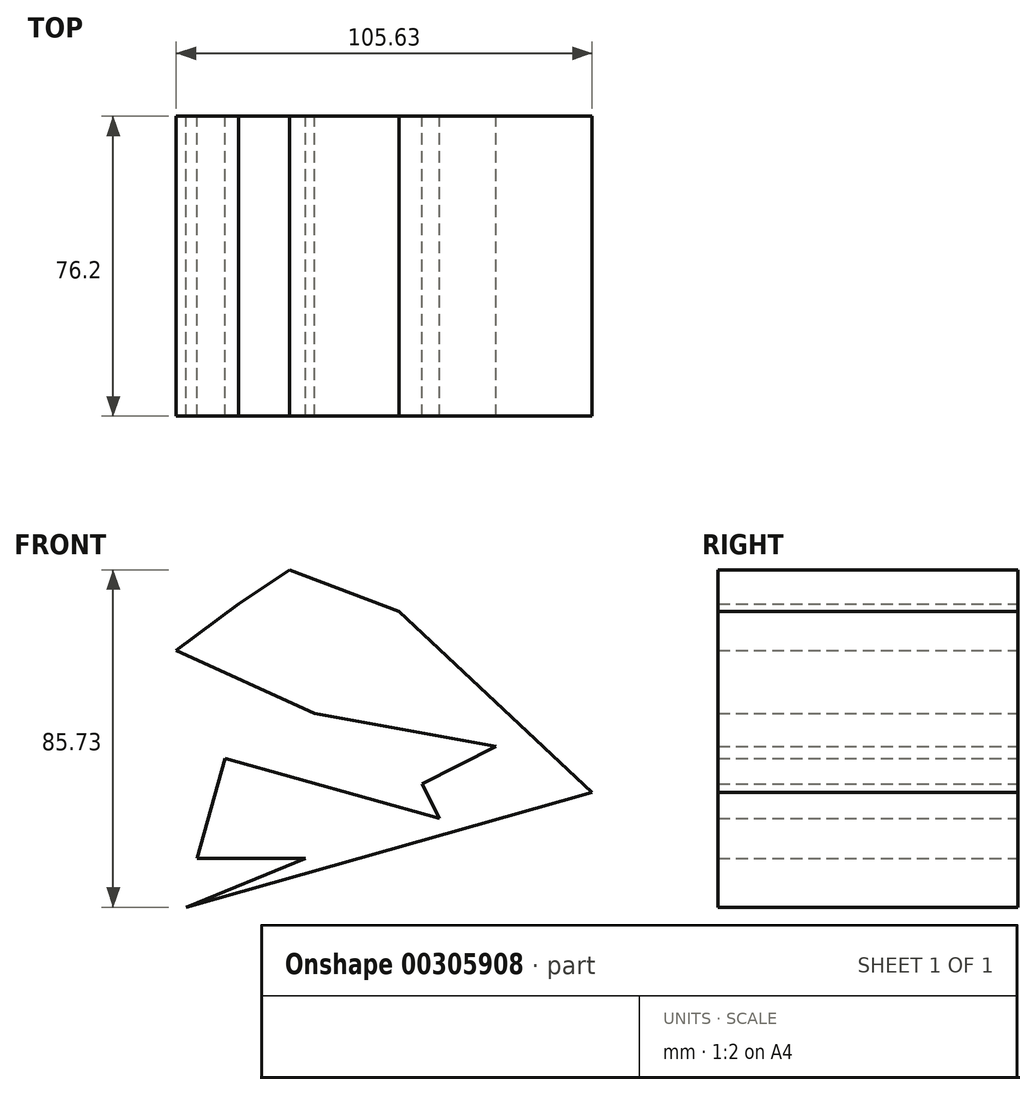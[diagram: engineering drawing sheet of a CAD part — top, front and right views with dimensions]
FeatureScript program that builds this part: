
annotation { "Feature Type Name" : "Feature", "Feature Type Description" : "" }
export const myFeature = defineFeature(function(context is Context, id is Id, definition is map)
    precondition{}
    {
        {
            var Q0;
            Q0=qCreatedBy(makeId("Front.planeOp"),FACE);
            var sketch = newSketch(context, id + "F0", { "sketchPlane" : qUnion([Q0])});
            skLineSegment(sketch, "E0", {"start": v(-44.24, -35.77) * mm, "end": v(58.83, -6.6) * mm});
            skLineSegment(sketch, "E1", {"start": v(58.83, -6.6) * mm, "end": v(9.75, 39.32) * mm});
            skLineSegment(sketch, "E2", {"start": v(9.75, 39.32) * mm, "end": v(-18.03, 49.96) * mm});
            skLineSegment(sketch, "E3", {"start": v(-18.03, 49.96) * mm, "end": v(-31.04, 41.29) * mm});
            skLineSegment(sketch, "E4", {"start": v(-31.04, 41.29) * mm, "end": v(-46.8, 29.46) * mm});
            skLineSegment(sketch, "E5", {"start": v(-46.8, 29.46) * mm, "end": v(-11.73, 13.5) * mm});
            skLineSegment(sketch, "E6", {"start": v(-11.73, 13.5) * mm, "end": v(34.4, 5.03) * mm});
            skLineSegment(sketch, "E7", {"start": v(34.4, 5.03) * mm, "end": v(15.67, -4.43) * mm});
            skLineSegment(sketch, "E8", {"start": v(15.67, -4.43) * mm, "end": v(20.12, -13.25) * mm});
            skLineSegment(sketch, "E9", {"start": v(20.12, -13.25) * mm, "end": v(-34.4, 2.07) * mm});
            skLineSegment(sketch, "E10", {"start": v(-34.4, 2.07) * mm, "end": v(-41.55, -23.41) * mm});
            skLineSegment(sketch, "E11", {"start": v(-41.55, -23.41) * mm, "end": v(-13.9, -23.41) * mm});
            skLineSegment(sketch, "E12", {"start": v(-13.9, -23.41) * mm, "end": v(-44.24, -35.77) * mm});
            skSolve(sketch);
        }
        {
            var Q0;
            Q0=makeQuery(id+"F0.imprint","IMPRINT",FACE,{"disambiguationData":[TD([[makeQuery(id+"F0.imprint","IMPRINT",EDGE,{"derivedFrom":sQuery(id+"F0.wireOp",EDGE,"E0")}),1.0]])]});
            extrude(context, id + "F1", {"entities" : qUnion([Q0]), "depth" : 76.2 * mm, "offsetDistance" : 25.4 * mm});
        }
    });
